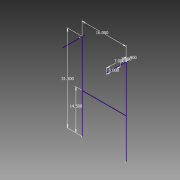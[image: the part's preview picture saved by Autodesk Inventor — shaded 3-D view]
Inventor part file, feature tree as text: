
AUTODESK INVENTOR PART (.ipt)
format: ipt  version: 2013 (Build 170138000, 138)  size: 70,656 bytes
history: native  units: in
note: dims shown in document units (in); Inventor stores cm internally (conversion verified against a paired STEP export)
features: sketch x3, plane x2
ambient origin geometry x8: Origin, YZ Plane, XZ Plane, XY Plane, X Axis, Y Axis, Z Axis, Center Point
feature tree (5):
  sketch  "Sketch1"  dims[d0=31.5in]
  plane  "Work Plane1"
  sketch  "Sketch2"  dims[d1=16.0in]
  plane  "Work Plane2"
  sketch  "Sketch3"  dims[d2=14.5in d3=0.9in d4=3.0in d5=5.0in d6=7.0in]
